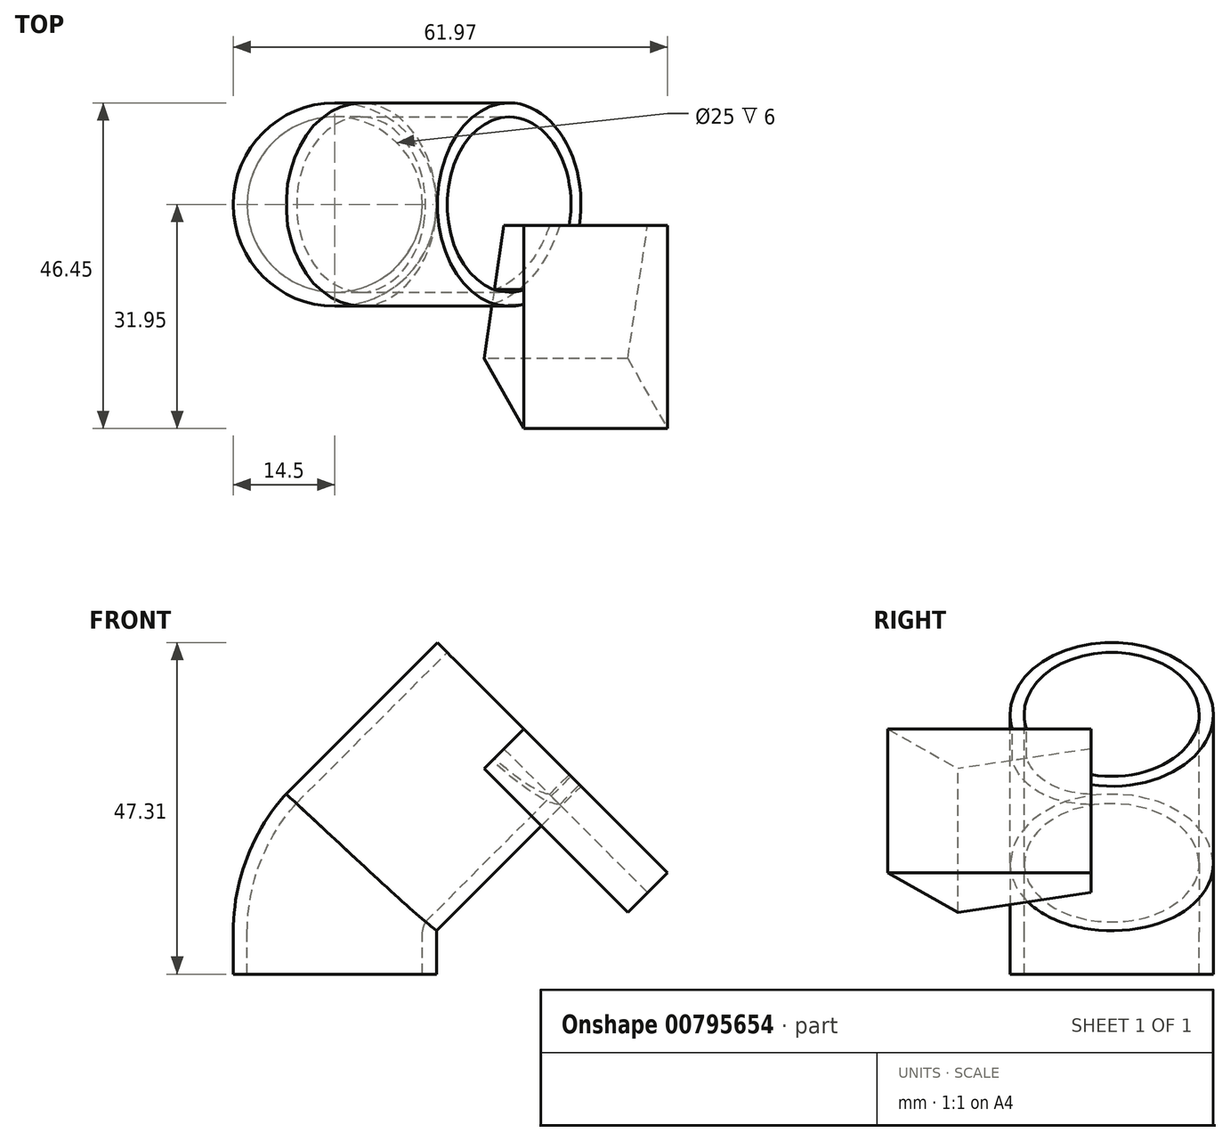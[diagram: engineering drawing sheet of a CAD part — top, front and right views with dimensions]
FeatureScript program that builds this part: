
annotation { "Feature Type Name" : "Feature", "Feature Type Description" : "" }
export const myFeature = defineFeature(function(context is Context, id is Id, definition is map)
    precondition{}
    {
        {
            var Q0;
            Q0=qCreatedBy(makeId("Front.planeOp"),FACE);
            var sketch = newSketch(context, id + "F0", { "sketchPlane" : qUnion([Q0])});
            skLineSegment(sketch, "E0", {"start": v(12.37, 37.05) * mm, "end": v(-8.84, 15.84) * mm});
            skLineSegment(sketch, "E1", {"start": v(-12.5, 0) * mm, "end": v(-12.5, 3.5) * mm});
            skLineSegment(sketch, "E2", {"start": v(-12.5, 0) * mm, "end": v(-12.5, 6) * mm});
            skArc(sketch, "E3", {"start": v(-12.5, 6) * mm, "mid": v(-11.56, 11.25) * mm, "end": v(-8.84, 15.84) * mm});
            skSolve(sketch);
        }
        {
            var Q0;
            Q0=sQuery(id+"F0.wireOp",EDGE,"E2");
            var Q1;
            Q1=sQuery(id+"F0.wireOp",VERTEX,"E1.start");
            cPlane(context, id + "F1", {"entities" : qUnion([Q0, Q1]), "cplaneType" : CPlaneType.CURVE_POINT, "offset" : 25 * mm, "width" : 150 * mm, "height" : 150 * mm});
        }
        {
            var Q0;
            Q0=qCreatedBy(id+"F1.planeOp",FACE);
            var sketch = newSketch(context, id + "F2", { "sketchPlane" : qUnion([Q0])});
            skPoint(sketch, "E4.0", {"position": v(-12.5, 0) * mm});
            skCircle(sketch, "E5", {"center": v(-12.5, 0) * mm, "radius": 12.5 * mm});
            skCircle(sketch, "E6", {"center": v(-12.5, 0) * mm, "radius": 14.5 * mm});
            skSolve(sketch);
        }
        {
            var Q0;
            Q0=makeQuery(id+"F2.imprint","IMPRINT",FACE,{"disambiguationData":[TD([[makeQuery(id+"F2.imprint","IMPRINT",EDGE,{"derivedFrom":sQuery(id+"F2.wireOp",EDGE,"E5")}),-1.0]])]});
            var Q1;
            Q1=sQuery(id+"F0.wireOp",EDGE,"E2");
            var Q2;
            Q2=sQuery(id+"F0.wireOp",EDGE,"E3");
            var Q3;
            Q3=sQuery(id+"F0.wireOp",EDGE,"E0");
            sweep(context, id + "F3", {"profiles" : qUnion([Q0]), "path" : qUnion([Q1, Q2, Q3])});
        }
        {
            var Q0;
            Q0=makeQuery(id+"F3.opSweep","CAP_FACE",FACE,{"disambiguationData":[OSD([sQuery(id+"F0.wireOp",VERTEX,"E0.start"),sQuery(id+"F2.wireOp",EDGE,"E5"),sQuery(id+"F2.wireOp",EDGE,"E6")])],"isStart":false});
            cPlane(context, id + "F4", {"entities" : qUnion([Q0]), "cplaneType" : CPlaneType.OFFSET, "offset" : 0 * mm, "width" : 150 * mm, "height" : 150 * mm});
        }
        {
            var Q0;
            Q0=qCreatedBy(id+"F4.planeOp",FACE);
            var sketch = newSketch(context, id + "F5", { "sketchPlane" : qUnion([Q0])});
            skPoint(sketch, "E7.0", {"position": v(-17.45, 0) * mm});
            skLineSegment(sketch, "E8.bottom", {"start": v(-2.95, -14.5) * mm, "end": v(-31.95, -14.5) * mm});
            skLineSegment(sketch, "E8.top", {"start": v(-2.95, 14.5) * mm, "end": v(-31.95, 14.5) * mm});
            skLineSegment(sketch, "E8.left", {"start": v(-2.95, -14.5) * mm, "end": v(-2.95, 14.5) * mm});
            skLineSegment(sketch, "E8.right", {"start": v(-31.95, -14.5) * mm, "end": v(-31.95, 14.5) * mm});
            skSolve(sketch);
        }
        {
            var Q0;
            Q0 = qSketchRegion(id + "F5", true);
            extrude(context, id + "F6", {"entities" : qUnion([Q0]), "oppositeDirection" : true, "depth" : 8 * mm, "offsetDistance" : 25 * mm});
        }
        {
            var Q0;
            Q0=makeQuery(id+"F6.opExtrude","CAP_EDGE",EDGE,{"disambiguationData":[OSD([sQuery(id+"F5.wireOp",EDGE,"E8.right")])],"isStart":false});
            chamfer(context, id + "F7", {"entities" : qUnion([Q0]), "chamferType" : ChamferType.TWO_OFFSETS, "width1" : 10 * mm, "oppositeDirection" : false, "width2" : 8 * mm, "tangentPropagation" : true});
        }
        {
            var Q0;
            Q0=makeQuery(id+"F6.opExtrude","CAP_EDGE",EDGE,{"disambiguationData":[OSD([sQuery(id+"F5.wireOp",EDGE,"E8.left")])],"isStart":false});
            chamfer(context, id + "F8", {"entities" : qUnion([Q0]), "chamferType" : ChamferType.TWO_OFFSETS, "width1" : 4 * mm, "oppositeDirection" : false, "width2" : 19 * mm, "tangentPropagation" : true});
        }
        {
            var Q0;
            Q0=makeQuery(id+"F6.opExtrude","SWEPT_BODY",BODY,{"disambiguationData":[OSD([sQuery(id+"F5.wireOp",EDGE,"E8.bottom"),sQuery(id+"F5.wireOp",EDGE,"E8.top"),sQuery(id+"F5.wireOp",EDGE,"E8.left"),sQuery(id+"F5.wireOp",EDGE,"E8.right")])]});
            var Q1;
            Q1=makeQuery(id+"F3.opSweep","SWEPT_BODY",BODY,{"disambiguationData":[OSD([sQuery(id+"F0.wireOp",EDGE,"E0"),sQuery(id+"F2.wireOp",EDGE,"E5"),sQuery(id+"F2.wireOp",EDGE,"E6")])]});
            booleanBodies(context, id + "F9", {"operationType" : BooleanOperationType.SUBTRACTION, "tools" : qUnion([Q0]), "targets" : qUnion([Q1]), "keepTools" : true});
        }
    });
